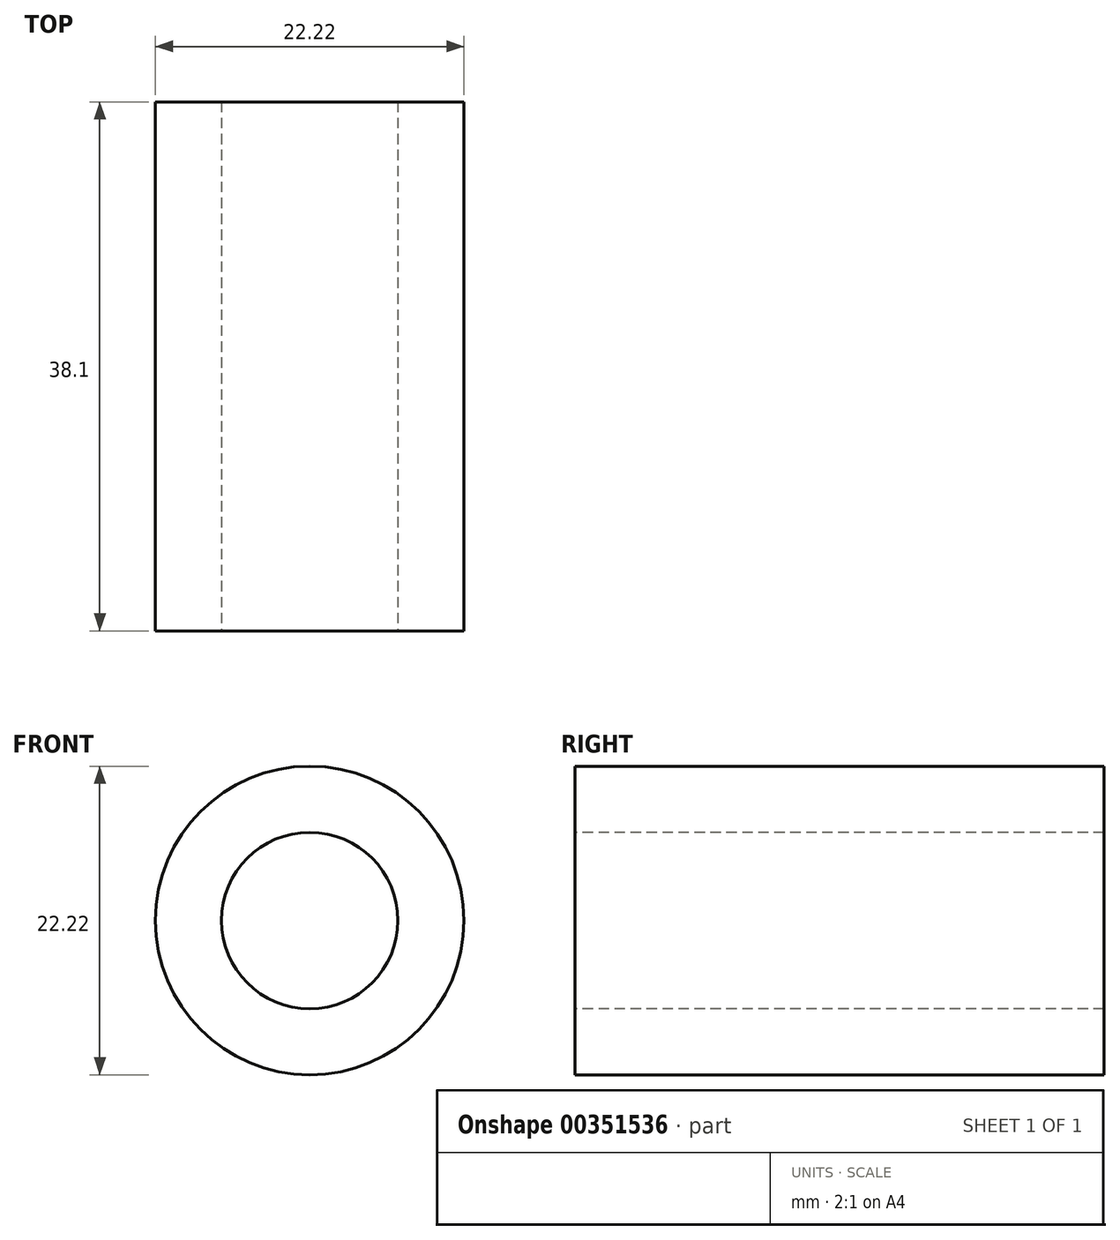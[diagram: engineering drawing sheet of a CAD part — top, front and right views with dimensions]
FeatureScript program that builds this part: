
annotation { "Feature Type Name" : "Feature", "Feature Type Description" : "" }
export const myFeature = defineFeature(function(context is Context, id is Id, definition is map)
    precondition{}
    {
        {
            var Q0;
            Q0=qCreatedBy(makeId("Front.planeOp"),FACE);
            var sketch = newSketch(context, id + "F0", { "sketchPlane" : qUnion([Q0])});
            skCircle(sketch, "E0", {"center": v(0, 0) * mm, "radius": 11.11 * mm});
            skSolve(sketch);
        }
        {
            var Q0;
            Q0 = qSketchRegion(id + "F0", true);
            extrude(context, id + "F1", {"entities" : qUnion([Q0]), "depth" : 38.1 * mm, "symmetric" : true});
        }
        {
            var Q0;
            Q0=makeQuery(id+"F1.opExtrude","CAP_FACE",FACE,{"disambiguationData":[OSD([sQuery(id+"F0.wireOp",EDGE,"E0")])],"isStart":false});
            var sketch = newSketch(context, id + "F2", { "sketchPlane" : qUnion([Q0])});
            skCircle(sketch, "E1", {"center": v(0, 0) * mm, "radius": 6.35 * mm});
            skSolve(sketch);
        }
        {
            var Q0;
            Q0 = qSketchRegion(id + "F2", true);
            extrude(context, id + "F3", {"entities" : qUnion([Q0]), "operationType" : NewBodyOperationType.REMOVE, "endBound" : BoundingType.THROUGH_ALL, "oppositeDirection" : true, "depth" : 25.4 * mm});
        }
    });
